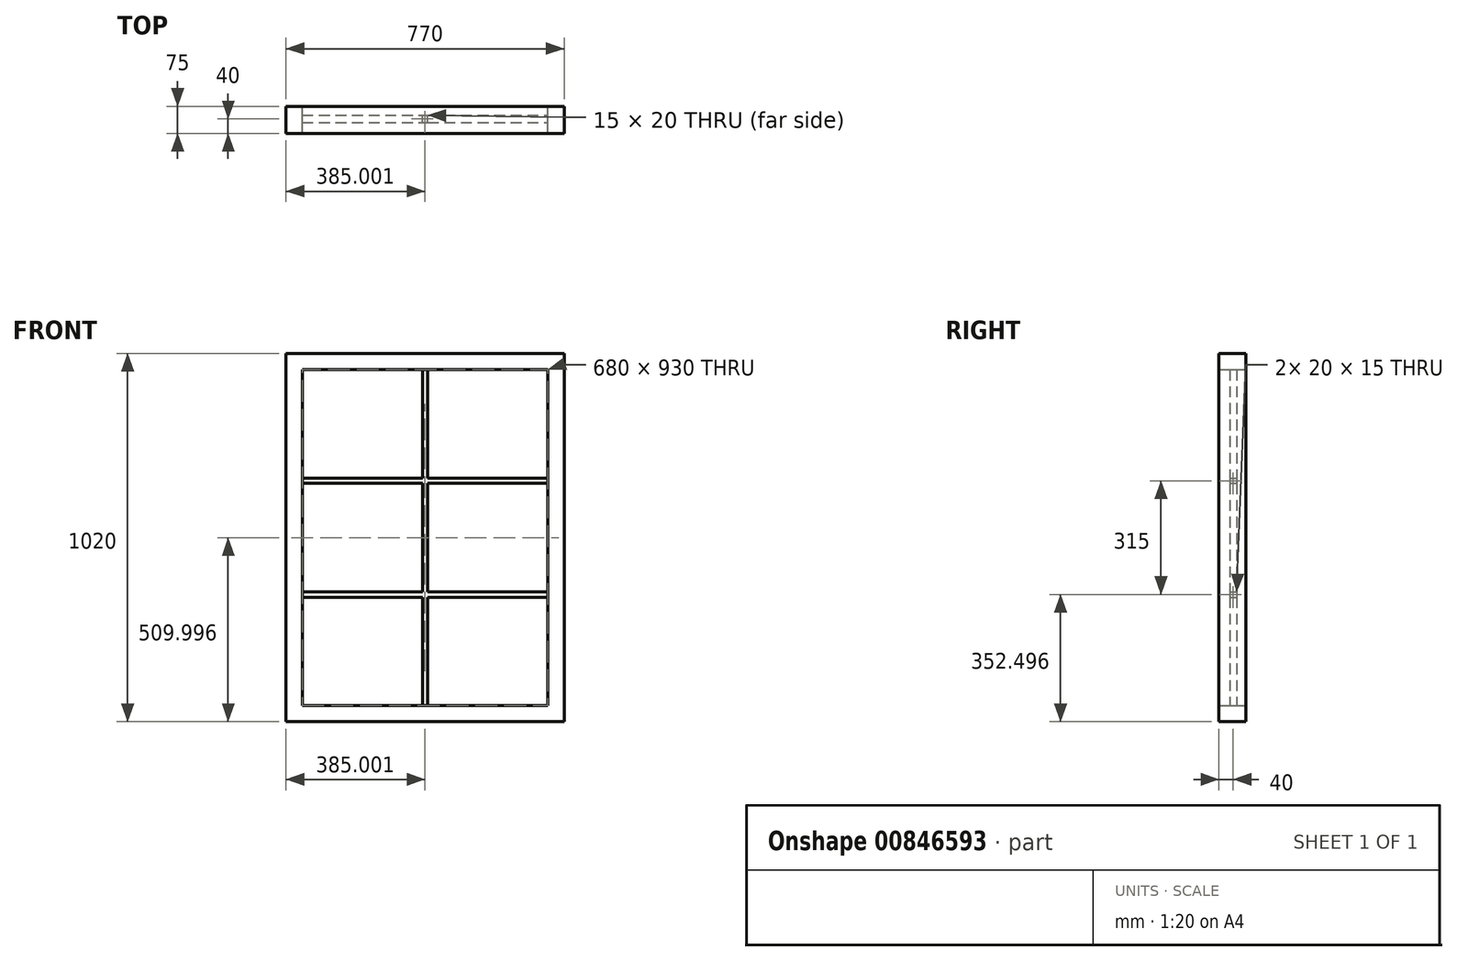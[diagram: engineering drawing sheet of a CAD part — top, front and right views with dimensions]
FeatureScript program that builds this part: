
annotation { "Feature Type Name" : "Feature", "Feature Type Description" : "" }
export const myFeature = defineFeature(function(context is Context, id is Id, definition is map)
    precondition{}
    {
        {
            var Q0;
            Q0=qCreatedBy(makeId("Front.planeOp"),FACE);
            var sketch = newSketch(context, id + "F0", { "sketchPlane" : qUnion([Q0])});
            skLineSegment(sketch, "E0.bottom", {"start": v(-388.14, 502.28) * mm, "end": v(381.86, 502.28) * mm});
            skLineSegment(sketch, "E0.top", {"start": v(-388.14, -517.72) * mm, "end": v(381.86, -517.72) * mm});
            skLineSegment(sketch, "E0.left", {"start": v(-388.14, 502.28) * mm, "end": v(-388.14, -517.72) * mm});
            skLineSegment(sketch, "E0.right", {"start": v(381.86, 502.28) * mm, "end": v(381.86, -517.72) * mm});
            skLineSegment(sketch, "E1.bottom", {"start": v(-343.14, 457.28) * mm, "end": v(336.86, 457.28) * mm});
            skLineSegment(sketch, "E1.top", {"start": v(-343.14, -472.72) * mm, "end": v(336.86, -472.72) * mm});
            skLineSegment(sketch, "E1.left", {"start": v(-343.14, 457.28) * mm, "end": v(-343.14, -472.72) * mm});
            skLineSegment(sketch, "E1.right", {"start": v(336.86, 457.28) * mm, "end": v(336.86, -472.72) * mm});
            skSolve(sketch);
        }
        {
            var Q0;
            Q0 = qSketchRegion(id + "F0", true);
            extrude(context, id + "F1", {"entities" : qUnion([Q0]), "depth" : 50 * mm, "offsetDistance" : 25 * mm, "hasSecondDirection" : true, "secondDirectionOppositeDirection" : true, "secondDirectionDepth" : 25 * mm});
        }
        {
            var Q0;
            Q0=qCreatedBy(makeId("Front.planeOp"),FACE);
            var sketch = newSketch(context, id + "F2", { "sketchPlane" : qUnion([Q0])});
            skLineSegment(sketch, "E2.bottom", {"start": v(-10.64, 457.28) * mm, "end": v(4.36, 457.28) * mm});
            skLineSegment(sketch, "E2.top", {"start": v(-10.64, -472.72) * mm, "end": v(4.36, -472.72) * mm});
            skLineSegment(sketch, "E2.left", {"start": v(-10.64, 457.28) * mm, "end": v(-10.64, 157.28) * mm});
            skLineSegment(sketch, "E2.right", {"start": v(4.36, 457.28) * mm, "end": v(4.36, 157.28) * mm});
            skLineSegment(sketch, "E3.bottom", {"start": v(-343.14, 157.28) * mm, "end": v(-10.64, 157.28) * mm});
            skLineSegment(sketch, "E3.top", {"start": v(-343.14, 142.28) * mm, "end": v(-10.64, 142.28) * mm});
            skLineSegment(sketch, "E3.left", {"start": v(-343.14, 157.28) * mm, "end": v(-343.14, 142.28) * mm});
            skLineSegment(sketch, "E3.right", {"start": v(336.86, 157.28) * mm, "end": v(336.86, 142.28) * mm});
            skLineSegment(sketch, "E4.bottom", {"start": v(-343.14, -157.72) * mm, "end": v(-10.64, -157.72) * mm});
            skLineSegment(sketch, "E4.top", {"start": v(-343.14, -172.72) * mm, "end": v(-10.64, -172.72) * mm});
            skLineSegment(sketch, "E4.left", {"start": v(-343.14, -157.72) * mm, "end": v(-343.14, -172.72) * mm});
            skLineSegment(sketch, "E4.right", {"start": v(336.86, -157.72) * mm, "end": v(336.86, -172.72) * mm});
            skLineSegment(sketch, "E5.trimOffspring", {"start": v(4.36, 157.28) * mm, "end": v(336.86, 157.28) * mm});
            skLineSegment(sketch, "E6.trimOffspring", {"start": v(-10.64, 142.28) * mm, "end": v(-10.64, -157.72) * mm});
            skLineSegment(sketch, "E7.trimOffspring", {"start": v(4.36, 142.28) * mm, "end": v(336.86, 142.28) * mm});
            skLineSegment(sketch, "E8.trimOffspring", {"start": v(4.36, 142.28) * mm, "end": v(4.36, -157.72) * mm});
            skLineSegment(sketch, "E9.trimOffspring", {"start": v(4.36, -172.72) * mm, "end": v(336.86, -172.72) * mm});
            skLineSegment(sketch, "E10.trimOffspring", {"start": v(4.36, -157.72) * mm, "end": v(336.86, -157.72) * mm});
            skLineSegment(sketch, "E11.trimOffspring", {"start": v(-10.64, -172.72) * mm, "end": v(-10.64, -472.72) * mm});
            skLineSegment(sketch, "E12.trimOffspring", {"start": v(4.36, -172.72) * mm, "end": v(4.36, -472.72) * mm});
            skSolve(sketch);
        }
        {
            var Q0;
            Q0 = qSketchRegion(id + "F2", true);
            extrude(context, id + "F3", {"entities" : qUnion([Q0]), "operationType" : NewBodyOperationType.ADD, "depth" : 20 * mm, "offsetDistance" : 25 * mm});
        }
    });
